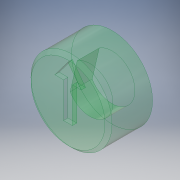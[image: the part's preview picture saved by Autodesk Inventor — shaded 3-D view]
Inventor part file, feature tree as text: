
AUTODESK INVENTOR PART (.ipt)
format: ipt  version: 2017 SP1 (Build 210196100, 196)  size: 157,696 bytes
history: native  units: in
note: dims shown in document units (in); Inventor stores cm internally (conversion verified against a paired STEP export)
features: extrude x5, sketch x5, projected_geometry x3, chamfer x1
ambient origin geometry x8: Origin, YZ Plane, XZ Plane, XY Plane, X Axis, Y Axis, Z Axis, Center Point
bodies: Solid1 (feature_tree)
feature tree (14):
  extrude  "Extrusion1"  Depth=0.0125in
  extrude  "Extrusion2"  Depth=0.1in
  extrude  "Extrusion3"  Depth=0.2in
  extrude  "Extrusion4"  Depth=0.05in
  extrude  "Extrusion5"  Depth=0.025in TaperAngle=0.0deg
  chamfer  "Chamfer1"  Angle=60.0deg  [1 undecoded]
  sketch  "Sketch1"  dims[d0=0.235in d2=0.0125in]
  sketch  "Sketch2"  dims[d3=1.0in d4=0.0in d5=0.1in]
  sketch  "Sketch3"  dims[d6=0.125in d7=0.0in d8=0.2in]
  sketch  "Sketch4"  dims[d9=0.1in d10=0.05in]
  projected_geometry  "Projected Loop1"
  projected_geometry  "Projected Loop2"
  sketch  "Sketch5"  dims[d11=0.15in d12=0.025in d13=0.0in d14=60.0deg d15=0.225in d16=0.4in d17=0.0in d18=0.25in d19=0.0in d20=0.02in d21=0.125in d22=45.0deg]
  projected_geometry  "Projected Loop3"
note: 1 required parameter value undecoded (feature->parameter linkage not recoverable at this tier; creation-order binding heuristic only, values carry confidence <= 0.55)
